# Revit family: Landscape-Forms_Lo-Glo_Path-Light
name_source: partatom
category: Lighting Fixtures
units: mm (PartAtom-declared; Revit-internal decimal feet)

## family parameters
Always vertical = Yes
Cut with Voids When Loaded = No
Light Source = Yes
OmniClass Number = 23.80.70.14.21
OmniClass Title = Street and Roadway Lighting
Part Type = Normal
Room Calculation Point = No
Round Connector Dimension = Use Diameter
Shared = No
Work Plane-Based = No

## types (1)
- GL-T4-40F
    Apparent Load = 0 VA
    Assembly Code = D5020280
    Color Filter = 16777215
    Default Elevation = 0' - 0"
    Description = Lo-Glo Path Light
    Diffuser Lens = LANDSCAPE FORMS - DIFFUSER - ILLUMINATED - OPAQUE
    Dimming Lamp Color Temperature Shift = <None>
    Height = 3' - 3"
    Lamp = LED Cartridge
    Load Classification = Lighting - Exterior
    Manufacturer = Landscape Forms
    Model = GL-T4-40F
    Number of Poles = 1
    Photometric Web File = LF_Lo-Glo_GL006L4-035F-40K.ies
    Tilt Angle = 90.00°
    URL = https://www.landscapeforms.com
    Voltage = 120 V
    Wattage Comments = 8

## geometry (parser evidence)
native form markers: Sweep x1
no freeform markers — native parametric forms only
